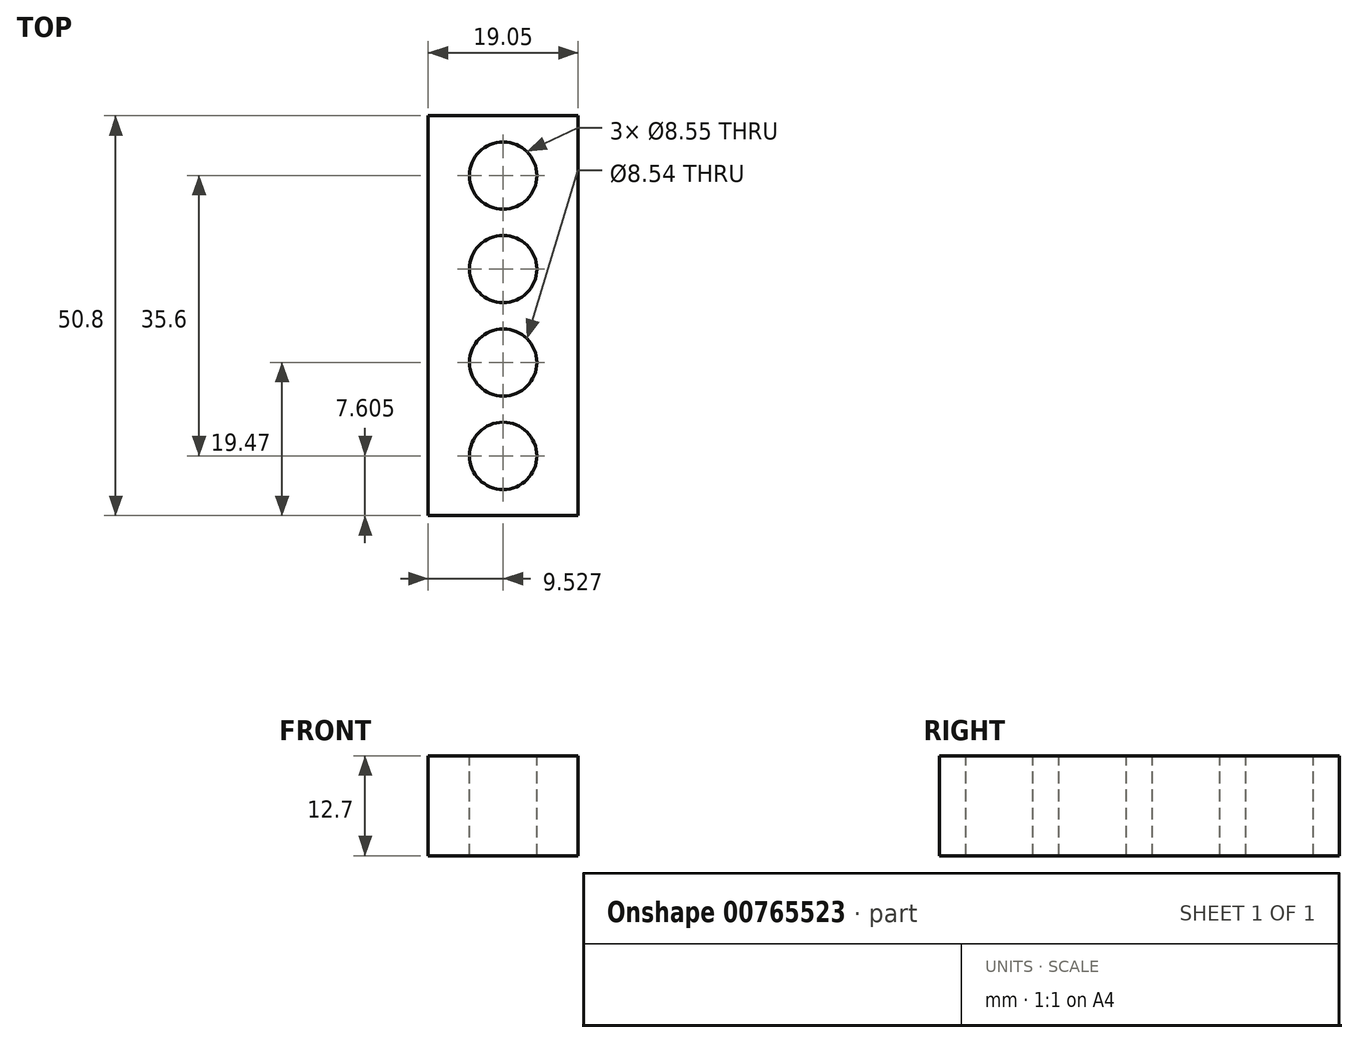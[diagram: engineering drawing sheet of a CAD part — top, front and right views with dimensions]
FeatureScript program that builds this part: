
annotation { "Feature Type Name" : "Feature", "Feature Type Description" : "" }
export const myFeature = defineFeature(function(context is Context, id is Id, definition is map)
    precondition{}
    {
        {
            var Q0;
            Q0=qCreatedBy(makeId("Top.planeOp"),FACE);
            var sketch = newSketch(context, id + "F0", { "sketchPlane" : qUnion([Q0])});
            skLineSegment(sketch, "E0.bottom", {"start": v(-133.46, -39.95) * mm, "end": v(-114.4, -39.95) * mm});
            skLineSegment(sketch, "E0.top", {"start": v(-133.46, 10.85) * mm, "end": v(-114.4, 10.85) * mm});
            skLineSegment(sketch, "E0.left", {"start": v(-133.46, -39.95) * mm, "end": v(-133.46, 10.85) * mm});
            skLineSegment(sketch, "E0.right", {"start": v(-114.4, -39.95) * mm, "end": v(-114.4, 10.85) * mm});
            skSolve(sketch);
        }
        {
            var Q0;
            Q0=makeQuery(id+"F0.imprint","IMPRINT",FACE,{"disambiguationData":[TD([[makeQuery(id+"F0.imprint","IMPRINT",EDGE,{"derivedFrom":sQuery(id+"F0.wireOp",EDGE,"E0.bottom")}),1.0]])]});
            extrude(context, id + "F1", {"entities" : qUnion([Q0]), "depth" : 12.7 * mm, "offsetDistance" : 25 * mm});
        }
        {
            var Q0;
            Q0=makeQuery(id+"F1.opExtrude","CAP_FACE",FACE,{"disambiguationData":[OSD([sQuery(id+"F0.wireOp",EDGE,"E0.bottom"),sQuery(id+"F0.wireOp",EDGE,"E0.top"),sQuery(id+"F0.wireOp",EDGE,"E0.left"),sQuery(id+"F0.wireOp",EDGE,"E0.right")])],"isStart":false});
            var sketch = newSketch(context, id + "F2", { "sketchPlane" : qUnion([Q0])});
            skLineSegment(sketch, "E1", {"start": v(-123.93, 10.85) * mm, "end": v(-123.93, 7.53) * mm});
            skLineSegment(sketch, "E2", {"start": v(-123.93, 7.53) * mm, "end": v(-123.93, 3.25) * mm});
            skCircle(sketch, "E3", {"center": v(-123.93, 3.25) * mm, "radius": 4.28 * mm});
            skLineSegment(sketch, "E4", {"start": v(-123.93, -1.02) * mm, "end": v(-123.93, -4.34) * mm});
            skLineSegment(sketch, "E5", {"start": v(-123.93, -4.34) * mm, "end": v(-123.93, -8.62) * mm});
            skCircle(sketch, "E6", {"center": v(-123.93, -8.62) * mm, "radius": 4.27 * mm});
            skLineSegment(sketch, "E7", {"start": v(-123.93, -12.9) * mm, "end": v(-123.93, -16.21) * mm});
            skLineSegment(sketch, "E8", {"start": v(-123.93, -16.21) * mm, "end": v(-123.93, -20.48) * mm});
            skCircle(sketch, "E9", {"center": v(-123.93, -20.48) * mm, "radius": 4.27 * mm});
            skLineSegment(sketch, "E10", {"start": v(-123.93, -24.75) * mm, "end": v(-123.93, -28.07) * mm});
            skLineSegment(sketch, "E11", {"start": v(-123.93, -28.07) * mm, "end": v(-123.93, -32.35) * mm});
            skCircle(sketch, "E12", {"center": v(-123.93, -32.35) * mm, "radius": 4.27 * mm});
            skSolve(sketch);
        }
        {
            var Q0;
            Q0=makeQuery(id+"F2.imprint","IMPRINT",FACE,{"disambiguationData":[TD([[makeQuery(id+"F2.imprint","IMPRINT",EDGE,{"derivedFrom":sQuery(id+"F2.wireOp",EDGE,"E12")}),1.0]])]});
            var Q1;
            {var subQ0=sQuery(id+"F2.wireOp",EDGE,"E9");var subQ1=makeQuery(id+"F2.imprint","IMPRINT",VERTEX,{"disambiguationData":[OD(0.0)],"derivedFrom":subQ0});Q1=makeQuery(id+"F2.imprint","IMPRINT",FACE,{"disambiguationData":[TD([[makeQuery(id+"F2.imprint","IMPRINT",EDGE,{"disambiguationData":[TD([[subQ1,-1.0]])],"derivedFrom":subQ0}),1.0]])]});}
            var Q2;
            {var subQ0=sQuery(id+"F2.wireOp",EDGE,"E6");var subQ1=makeQuery(id+"F2.imprint","IMPRINT",VERTEX,{"disambiguationData":[OD(0.0)],"derivedFrom":subQ0});Q2=makeQuery(id+"F2.imprint","IMPRINT",FACE,{"disambiguationData":[TD([[makeQuery(id+"F2.imprint","IMPRINT",EDGE,{"disambiguationData":[TD([[subQ1,-1.0]])],"derivedFrom":subQ0}),1.0]])]});}
            var Q3;
            {var subQ0=sQuery(id+"F2.wireOp",EDGE,"E3");var subQ1=makeQuery(id+"F2.imprint","IMPRINT",VERTEX,{"disambiguationData":[OD(0.0)],"derivedFrom":subQ0});Q3=makeQuery(id+"F2.imprint","IMPRINT",FACE,{"disambiguationData":[TD([[makeQuery(id+"F2.imprint","IMPRINT",EDGE,{"disambiguationData":[TD([[subQ1,-1.0]])],"derivedFrom":subQ0}),1.0]])]});}
            extrude(context, id + "F3", {"entities" : qUnion([Q0, Q1, Q2, Q3]), "operationType" : NewBodyOperationType.REMOVE, "oppositeDirection" : true, "depth" : 25 * mm, "offsetDistance" : 25 * mm});
        }
    });
